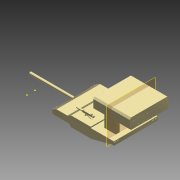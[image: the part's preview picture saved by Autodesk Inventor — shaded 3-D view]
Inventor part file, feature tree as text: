
AUTODESK INVENTOR PART (.ipt)
format: ipt  version: 2015 (Build 190159000, 159)  size: 836,096 bytes
history: native  units: in
note: dims shown in document units (in); Inventor stores cm internally (conversion verified against a paired STEP export)
features: sketch x13, extrude x8, projected_geometry x7, plane x4, hole x2, mirror x1, chamfer x1, other x1
ambient origin geometry x8: Origin, YZ Plane, XZ Plane, XY Plane, X Axis, Y Axis, Z Axis, Center Point
bodies: Solid1 (feature_tree)
feature tree (37):
  extrude  "Extrusion1"  Depth=3.0in
  extrude  "Extrusion2"  [1 undecoded]
  sketch  "Sketch4"  dims[d19=0.36in d20=0.75in d21=0.375in d22=0.25in d23=0.5635in d24=0.365in d25=0.0in d26=-0.5625in]
  sketch  "Sketch5"  dims[d27=0.1in d28=90.0deg]
  hole  "Hole2"  [1 undecoded]
  plane  "Work Plane2"
  extrude  "Extrusion3"  [1 undecoded]
  plane  "Work Plane3"
  mirror  "Mirror1"
  sketch  "Sketch9"  dims[d34=0.4775in d35=0.477in]
  sketch  "Sketch10"  dims[d36=0.2673in d37=0.267in d38=1.0in d39=0.0in]
  extrude  "Extrusion4"  Depth=0.477in
  plane  "Work Plane4"
  extrude  "Extrusion5"  Depth=0.267in
  chamfer  "Chamfer1"  Distance=1.0in
  extrude  "Extrusion6"  Depth=2.5in
  extrude  "Extrusion7"  Depth=0.336in
  extrude  "Extrusion8"  Depth=0.336in
  hole  "Hole3"  [1 undecoded]
  sketch  "Sketch1"  dims[d2=3.0in d3=0.0in d5=1.5in]
  other  "Image1"
  sketch  "Sketch2"  dims[d6=3.0in d7=0.0in]
  projected_geometry  "Projected Loop3"
  projected_geometry  "Projected Loop4"
  plane  "Work Plane1"
  sketch  "Sketch7"  dims[d29=0.1in d30=0.0in d31=-0.875in]
  sketch  "Sketch11"  dims[d42=2.5in d43=0.3364in]
  sketch  "Sketch12"  dims[d44=0.336in d45=0.336in]
  sketch  "Sketch13"  dims[d46=0.336in d47=0.336in]
  sketch  "Sketch14"  dims[d48=0.336in d49=0.336in]
  projected_geometry  "Projected Loop5"
  sketch  "Sketch15"  dims[d50=0.336in]
  projected_geometry  "Projected Loop6"
  projected_geometry  "Projected Loop7"
  projected_geometry  "Projected Loop8"
  sketch  "Sketch16"  dims[d51=0.168in d52=0.185in d54=2.5in d55=0.0in d56=0.1in d57=0.125in d58=45.0deg d59=0.001in d60=0.0in d61=0.4in d62=0.4in d63=0.2in d64=0.2in d65=0.03in d66=0.0in d67=0.4in d68=0.4in d69=0.165in d70=0.165in d71=0.165in d72=0.03in d73=0.0in d74=0.15in d75=0.75in d76=0.119in d77=0.25in d78=0.5635in d79=3.8in d80=0.0in]
  projected_geometry  "Projected Loop9"
note: 4 required parameter values undecoded (feature->parameter linkage not recoverable at this tier; creation-order binding heuristic only, values carry confidence <= 0.55)
